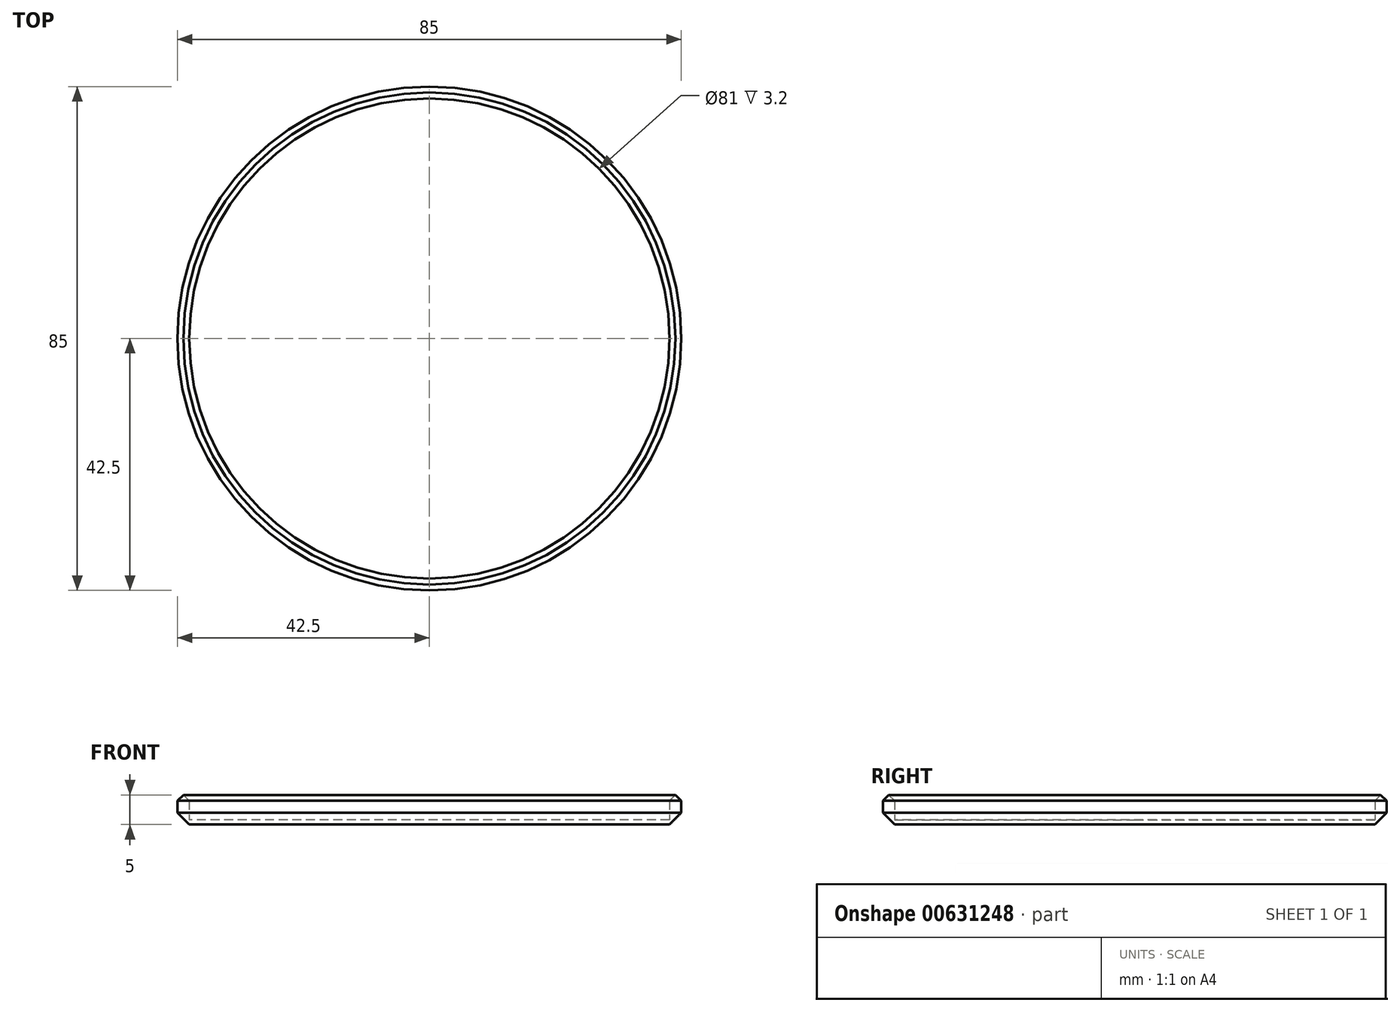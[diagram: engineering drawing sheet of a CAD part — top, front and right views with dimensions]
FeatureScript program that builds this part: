
annotation { "Feature Type Name" : "Feature", "Feature Type Description" : "" }
export const myFeature = defineFeature(function(context is Context, id is Id, definition is map)
    precondition{}
    {
        {
            var Q0;
            Q0=qCreatedBy(makeId("Top.planeOp"),FACE);
            var sketch = newSketch(context, id + "F0", { "sketchPlane" : qUnion([Q0])});
            skCircle(sketch, "E0", {"center": v(0, 0) * mm, "radius": 40.5 * mm});
            skCircle(sketch, "E1.0", {"center": v(0, 0) * mm, "radius": 42.5 * mm});
            skSolve(sketch);
        }
        {
            var Q0;
            Q0=makeQuery(id+"F0.imprint","IMPRINT",FACE,{"disambiguationData":[TD([[makeQuery(id+"F0.imprint","IMPRINT",EDGE,{"derivedFrom":sQuery(id+"F0.wireOp",EDGE,"E0")}),1.0]])]});
            extrude(context, id + "F1", {"entities" : qUnion([Q0]), "depth" : .8 * mm, "offsetDistance" : 25 * mm});
        }
        {
            var Q0;
            Q0=makeQuery(id+"F0.imprint","IMPRINT",FACE,{"disambiguationData":[TD([[makeQuery(id+"F0.imprint","IMPRINT",EDGE,{"derivedFrom":sQuery(id+"F0.wireOp",EDGE,"E0")}),-1.0]])]});
            extrude(context, id + "F2", {"entities" : qUnion([Q0]), "operationType" : NewBodyOperationType.ADD, "depth" : 5 * mm, "offsetDistance" : 25 * mm});
        }
        {
            var Q0;
            Q0=makeQuery(id+"F2.opExtrude","CAP_EDGE",EDGE,{"disambiguationData":[OSD([sQuery(id+"F0.wireOp",EDGE,"E1.0")])],"isStart":true});
            chamfer(context, id + "F3", {"entities" : qUnion([Q0]), "width" : 2 * mm, "tangentPropagation" : true});
        }
        {
            var Q0;
            Q0=makeQuery(id+"F2.opExtrude","CAP_EDGE",EDGE,{"disambiguationData":[OSD([sQuery(id+"F0.wireOp",EDGE,"E0")])],"isStart":false});
            var Q1;
            Q1=makeQuery(id+"F2.opExtrude","CAP_EDGE",EDGE,{"disambiguationData":[OSD([sQuery(id+"F0.wireOp",EDGE,"E1.0")])],"isStart":false});
            chamfer(context, id + "F4", {"entities" : qUnion([Q0, Q1]), "width" : 1 * mm, "tangentPropagation" : true});
        }
    });
